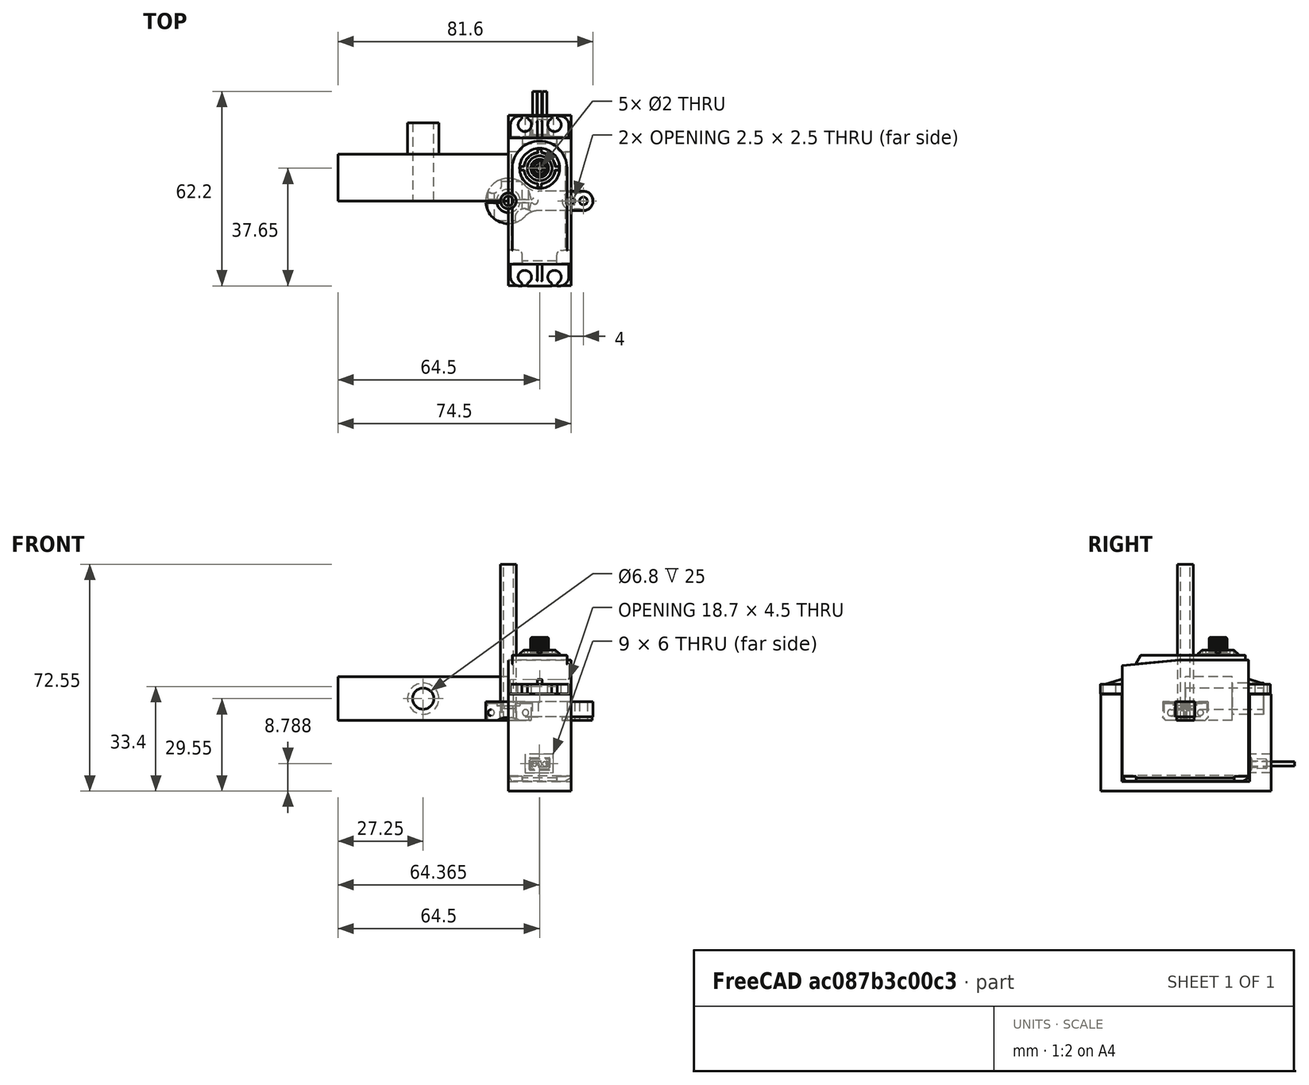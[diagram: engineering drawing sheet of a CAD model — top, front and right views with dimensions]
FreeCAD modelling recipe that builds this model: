
FCSTD DOCUMENT  (FreeCAD 0.19R24366 (Git))
Label: ServoSunFinderSF3218MG_v2
License: All rights reserved
LicenseURL: http://en.wikipedia.org/wiki/All_rights_reserved
objects: Sketcher::SketchObject×7, PartDesign::Pad×4, App::Part×4, PartDesign::Pocket×3, PartDesign::Body×3, Part::Feature×2, Mesh::Feature×1, App::MeasureDistance×1
note: 26 computed .brp shape members not serialized (recipe doc carries the construction recipe); baked Part::Feature solids carry a one-line shape summary decoded from their .brp

FEATURE [Part::Feature] Solid  label="Servo_SF3218MG"
  Placement = pos=(0,0,0) rot=(1,0,0;1.5708rad)
  shape: bbox 20 x 62.45 x 46.03 mm, 436 faces (baked)
FEATURE [Sketcher::SketchObject] Sketch  label="ServoHolder"
  FullyConstrained = false
  MapMode = 4
  Placement = pos=(0,0,0) rot=(0.57735,0.57735,0.57735;2.0944rad)
  sketch-geometry (8):
    g0: LineSegment StartX=-27.0989 StartY=-22.5482 StartZ=0 EndX=27.4011 EndY=-22.5482 EndZ=0
    g1: LineSegment StartX=20.6511 StartY=-19.5482 StartZ=0 EndX=20.6511 EndY=8.45178 EndZ=0
    g2: LineSegment StartX=20.6511 StartY=8.45178 StartZ=0 EndX=27.4011 EndY=8.45178 EndZ=0
    g3: LineSegment StartX=-20.3489 StartY=-19.5482 StartZ=0 EndX=-20.3489 EndY=8.45178 EndZ=0
    g4: LineSegment StartX=-20.3489 StartY=8.45178 StartZ=0 EndX=-27.0989 EndY=8.45178 EndZ=0
    g5: LineSegment StartX=20.6511 StartY=-19.5482 StartZ=0 EndX=-20.3489 EndY=-19.5482 EndZ=0
    g6: LineSegment StartX=-27.0989 StartY=8.45178 StartZ=0 EndX=-27.0989 EndY=-22.5482 EndZ=0
    g7: LineSegment StartX=27.4011 StartY=8.45178 StartZ=0 EndX=27.4011 EndY=-22.5482 EndZ=0
  constraints (22):
    c: Horizontal(g0)
    c: Coincident(g1,g2)
    c: Horizontal(g2)
    c: Vertical(g1)
    c: Coincident(g3,g4)
    c: Horizontal(g4)
    c: Vertical(g3)
    c: Coincident(g5,g1)
    c: Coincident(g5,g3)
    c: Horizontal(g5)
    c: Coincident(g6,g4)
    c: Coincident(g6,g0)
    c: Vertical(g6)
    c: Coincident(g7,g2)
    c: Coincident(g7,g0)
    c: Vertical(g7)
    c: DistanceX(g0,g0) = 54.5
    c: DistanceX(g5,g5) = 41
    c: Equal(g4,g2)
    c: Horizontal(g3,g1)
    c: DistanceY(g0,g1) = 3
    c: DistanceY(g1,g1) = 28
FEATURE [Sketcher::SketchObject] Sketch001  label="WireHoleSketch"
  FullyConstrained = false
  Placement = pos=(0,27.4011,0) rot=(0,0.707107,0.707107;3.14159rad)
  sketch-geometry (4):
    g0: LineSegment StartX=-5.36505 StartY=-10.7623 StartZ=0 EndX=-14.3651 EndY=-10.7623 EndZ=0
    g1: LineSegment StartX=-14.3651 StartY=-10.7623 StartZ=0 EndX=-14.3651 EndY=-16.7623 EndZ=0
    g2: LineSegment StartX=-14.3651 StartY=-16.7623 StartZ=0 EndX=-5.36505 EndY=-16.7623 EndZ=0
    g3: LineSegment StartX=-5.36505 StartY=-16.7623 StartZ=0 EndX=-5.36505 EndY=-10.7623 EndZ=0
  constraints (10):
    c: Coincident(g1,g2)
    c: Coincident(g2,g3)
    c: Coincident(g3,g0)
    c: Horizontal(g0)
    c: Horizontal(g2)
    c: Vertical(g1)
    c: Vertical(g3)
    c: Coincident(g1,g0)
    c: DistanceX(g0,g0) = 9
    c: DistanceY(g1,g1) = 6
FEATURE [PartDesign::Pad] Pad  label="ExtrudeServoHolder"
  Direction = (1,1,1)
  Length = 20
  Length2 = 100
  Placement = pos=(0,0,0) rot=(0.57735,0.57735,0.57735;2.0944rad)
  Profile = -> Sketch
  Type = 0
FEATURE [PartDesign::Pocket] Pocket
  BaseFeature = -> Pad
  Length = 8
  Length2 = 100
  Placement = pos=(0,0,0) rot=(0.57735,0.57735,0.57735;2.0944rad)
  Profile = -> Sketch001
  Type = 0
FEATURE [PartDesign::Body] Body
  Group = -> [Sketch001,Sketch,Pad,Pocket]
  Origin = -> Origin001
  Tip = -> Pocket
FEATURE [App::Part] Part  label="Servo_SF3218MG001"
  Group = -> [Solid,Body]
  Origin = -> Origin
FEATURE [Part::Feature] Solid001  label="ServoHorn"
  shape: bbox 34.33 x 14.81 x 6 mm, 52 faces (baked)
FEATURE [App::Part] Part002  label="ServoHorn001"
  Group = -> [Solid001]
  Origin = -> Origin004
FEATURE [Sketcher::SketchObject] Sketch007
  FullyConstrained = true
  MapMode = 5
  Support = -> [XY_Plane006]
  sketch-geometry (1):
    g0: Circle CenterX=0 CenterY=0 CenterZ=0 NormalX=0 NormalY=0 NormalZ=1 AngleXU=0 Radius=2.5
  constraints (2):
    c: Coincident(g0,g-1)
    c: Diameter(g0) = 5
FEATURE [PartDesign::Pad] Pad002
  Direction = (1,1,1)
  Length = 50
  Length2 = 100
  Profile = -> Sketch007
  Type = 0
FEATURE [Sketcher::SketchObject] Sketch008
  FullyConstrained = true
  MapMode = 5
  Placement = pos=(0,0,50) rot=(0,0,1;0rad)
  Support = -> [Pad002]
  sketch-geometry (1):
    g0: Circle CenterX=0 CenterY=0 CenterZ=0 NormalX=0 NormalY=0 NormalZ=1 AngleXU=0 Radius=1.5
  constraints (2):
    c: Coincident(g0,g-1)
    c: Diameter(g0) = 3
FEATURE [PartDesign::Pocket] Pocket003
  BaseFeature = -> Pad002
  Length = 75
  Length2 = 100
  Profile = -> Sketch008
  Type = 0
FEATURE [PartDesign::Body] Body002
  Group = -> [Sketch007,Pad002,Sketch008,Pocket003]
  Origin = -> Origin006
  Tip = -> Pocket003
FEATURE [App::Part] Part003  label="PostHoleJacket"
  Group = -> [Body002]
  Origin = -> Origin005
FEATURE [Sketcher::SketchObject] Sketch009
  FullyConstrained = true
  MapMode = 5
  Support = -> [XY_Plane008]
  sketch-geometry (4):
    g0: LineSegment StartX=0 StartY=0 StartZ=0 EndX=-54.5 EndY=0 EndZ=0
    g1: LineSegment StartX=-54.5 StartY=0 StartZ=0 EndX=-54.5 EndY=15 EndZ=0
    g2: LineSegment StartX=-54.5 StartY=15 StartZ=0 EndX=0 EndY=15 EndZ=0
    g3: LineSegment StartX=0 StartY=15 StartZ=0 EndX=0 EndY=0 EndZ=0
  constraints (11):
    c: Coincident(g0,g1)
    c: Coincident(g1,g2)
    c: Coincident(g2,g3)
    c: Coincident(g3,g0)
    c: Horizontal(g0)
    c: Horizontal(g2)
    c: Vertical(g1)
    c: Vertical(g3)
    c: Coincident(g0,g-1)
    c: DistanceX(g0,g0) = 54.5
    c: DistanceY(g1,g1) = 15
FEATURE [PartDesign::Pad] Pad003
  Direction = (1,1,1)
  Length = 14
  Length2 = 100
  Profile = -> Sketch009
  Type = 0
FEATURE [Sketcher::SketchObject] Sketch011
  ExternalGeometry = -> [Pad003]
  FullyConstrained = true
  MapMode = 5
  Placement = pos=(0,15,0) rot=(0,0.707107,0.707107;3.14159rad)
  Support = -> [Pad003]
  sketch-geometry (3):
    g0: Circle CenterX=27.25 CenterY=7 CenterZ=0 NormalX=0 NormalY=0 NormalZ=1 AngleXU=0 Radius=5
    g1: LineSegment StartX=27.25 StartY=7 StartZ=0 EndX=0 EndY=7 EndZ=0
    g2: LineSegment StartX=27.25 StartY=7 StartZ=0 EndX=54.5 EndY=7 EndZ=0
  constraints (9):
    c: Diameter(g0) = 10
    c: Coincident(g1,g0)
    c: PointOnObject(g1,g-5)
    c: Horizontal(g1)
    c: Coincident(g2,g0)
    c: PointOnObject(g2,g-4)
    c: Horizontal(g2)
    c: Equal(g1,g2)
    c: DistanceY(g0,g-4) = 7
FEATURE [PartDesign::Pad] Pad005
  BaseFeature = -> Pad003
  Direction = (1,1,1)
  Length = 10
  Length2 = 100
  Profile = -> Sketch011
  Type = 0
FEATURE [Mesh::Feature] Mesh  label="ServoHolderPart (Meshed)"
FEATURE [Sketcher::SketchObject] Sketch012
  ExternalGeometry = -> [Pad005]
  FullyConstrained = true
  MapMode = 5
  Placement = pos=(3e-15,25,-5.2e-15) rot=(0,0.707107,0.707107;3.14159rad)
  Support = -> [Pad005]
  sketch-geometry (1):
    g0: Circle CenterX=27.25 CenterY=7 CenterZ=0 NormalX=0 NormalY=0 NormalZ=1 AngleXU=0 Radius=3.4
  constraints (2):
    c: Coincident(g0,g-3)
    c: Diameter(g0) = 6.8
FEATURE [PartDesign::Pocket] Pocket004
  BaseFeature = -> Pad005
  Length = 30
  Length2 = 100
  Profile = -> Sketch012
  Type = 0
FEATURE [PartDesign::Body] Body003
  Group = -> [Sketch009,Pad003,Sketch011,Pad005,Sketch012,Pocket004]
  Origin = -> Origin008
  Tip = -> Pocket004
FEATURE [App::Part] Part004  label="ServoRudderHolderConnect"
  Group = -> [Body003]
  Origin = -> Origin007
FEATURE [App::MeasureDistance] Distance  label="Distance: 55.34 mm"
  Distance = 55.3433
  P1 = (51.8921,-27.0989,-22.5482)
  P2 = (42.2674,27.4011,-22.5482)
